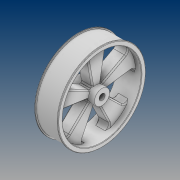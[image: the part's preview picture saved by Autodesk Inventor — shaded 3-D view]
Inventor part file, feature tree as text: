
AUTODESK INVENTOR PART (.ipt)
format: ipt  version: 2021 (Build 250183000, 183)  size: 374,272 bytes
history: native  units: mm
features: extrude x4, sketch x4, fillet x3, projected_geometry x3, mirror x2, chamfer x1
ambient origin geometry x8: Origin, YZ Plane, XZ Plane, XY Plane, X Axis, Y Axis, Z Axis, Center Point
bodies: Solid1 (feature_tree)
feature tree (17):
  extrude  "Extrusion1"  Depth=20.0mm
  extrude  "Extrusion2"  Depth=40.0mm TaperAngle=0.0deg
  extrude  "Extrusion3"  Depth=10.0mm
  mirror  "Mirror1"
  fillet  "Fillet1"  Radius=10.0mm
  fillet  "Fillet2"  Radius=3.490659mm
  chamfer  "Chamfer1"  Distance=50.0mm Angle=360.0deg
  extrude  "Extrusion4"  Depth=0.75mm TaperAngle=0.0deg
  mirror  "Mirror2"
  fillet  "Fillet3"  Radius=7.25mm
  sketch  "Sketch1"  dims[d0=10.0mm d1=20.0mm]
  sketch  "Sketch2"  dims[d2=141.0mm d3=40.0mm d4=0.0mm]
  projected_geometry  "Projected Loop1"
  sketch  "Sketch3"  dims[d5=5.0mm d6=25.0mm d7=10.0mm d8=0.0mm d11=3.490659mm]
  projected_geometry  "Projected Loop2"
  sketch  "Sketch4"  dims[d12=30.0mm d13=50.0mm d15=360.0deg d17=100.75mm d18=0.0mm d19=7.25mm d20=3.0mm d21=2.0mm d22=2.0mm d23=45.0deg d24=2.0mm d25=2.0mm d26=0.0mm d27=0.75mm]
  projected_geometry  "Projected Loop3"
